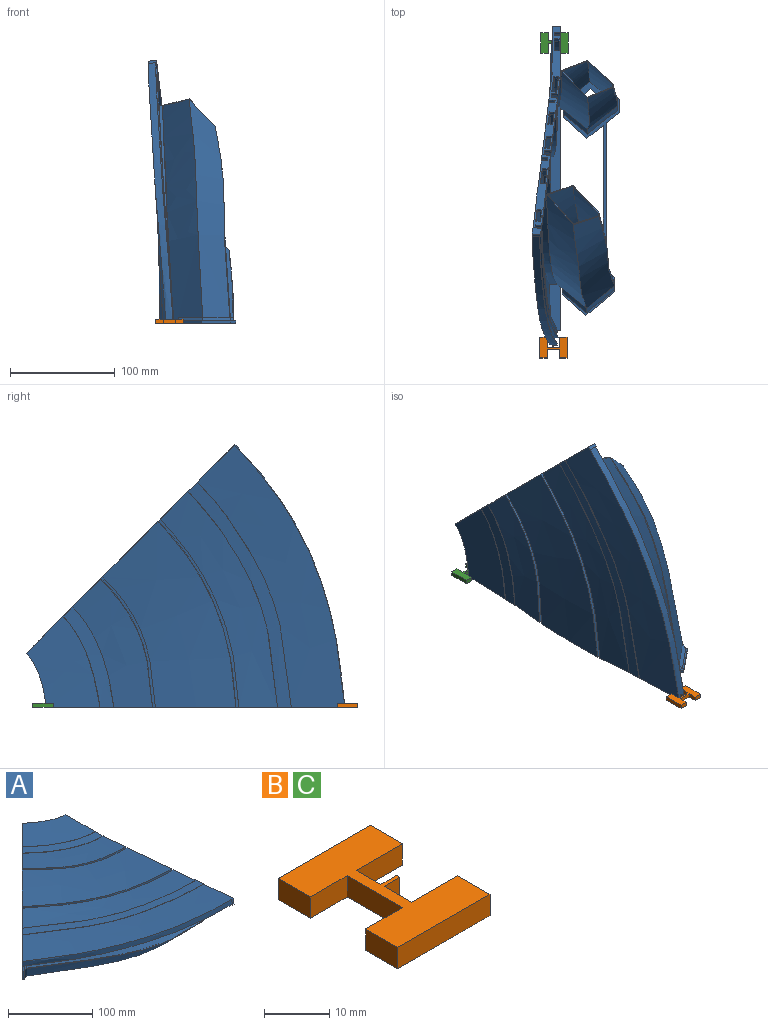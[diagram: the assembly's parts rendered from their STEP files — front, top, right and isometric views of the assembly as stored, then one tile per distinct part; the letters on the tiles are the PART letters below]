
ASSEMBLY  parts=3 mates=1
PART A: 239 faces, bbox 308.2x408.3x92.3 mm
  f0: plane 16.99x11.09mm, normal (0.56,0.56,-0.61), area 53.8mm2, adj f176,f189,f194,f237
  f1: plane 15.73x10.48mm, normal (-0.56,-0.56,-0.62), area 50mm2, adj f176,f194,f207,f237
  f2: plane 6.18x4.61mm, normal (-0.64,-0.76,0.07), area 18.6mm2, adj f3,f8,f93,f150,f234
  f3: bspline ~224.09x154.19mm, area 4266.2mm2, adj f2,f4,f5,f6,f38,f39,f93,f97
  f4: plane 6.18x4.61mm, normal (0.64,0.76,-0.07), area 18.6mm2, adj f3,f5,f6,f7,f234
  f5: plane 5.6x3.35mm, normal (0,-0.09,-1), area 13.8mm2, adj f3,f4,f6,f7,f96,f146
  f6: plane 0.35x0mm, normal (0,1,-0.09), area 0mm2, adj f3,f4,f5
  f7: plane 6.21x0.86mm, normal (-0.77,0.64,-0.06), area 2.6mm2, adj f4,f5,f96,f175
  f8: plane 6.37x2.71mm, normal (-0.77,0.64,-0.06), area 17.6mm2, adj f2,f93,f145,f174,f175
  f9: plane 6.18x4.77mm, normal (-0.71,-0.7,0.06), area 18.6mm2, adj f11,f13,f44,f233
  f10: plane 5.65x3mm, normal (0,-0.09,-1), area 13.5mm2, adj f44,f96,f148,f172,f232
  f11: plane 12.48x5.23mm, normal (0,-0.09,-1), area 30.1mm2, adj f9,f12,f13,f44,f156,f157
  f12: plane 9.48x0.11mm, normal (0,-1,0.09), area 0.1mm2, adj f11,f44,f157
  f13: plane 6.37x2.71mm, normal (-0.71,0.7,-0.06), area 19.1mm2, adj f9,f11,f43,f173
  f14: bspline ~224.09x118.25mm, area 679.4mm2, adj f15,f23,f28,f50,f111,f177,f229,f230
  f15: plane 0.65x0.19mm, normal (1,0,0), area 0.1mm2, adj f14,f26,f112,f229,f231
  f16: bspline ~224.09x143.33mm, area 3418.5mm2, adj f17,f26,f176,f182,f183,f209,f222,f223
  f17: bspline ~86.16x71.71mm, area 2834.7mm2, adj f16,f25,f223,f231
  f18: bspline ~224.09x141.31mm, area 2875.5mm2, adj f19,f24,f211,f231
  f19: bspline ~224.09x142.44mm, area 3385.1mm2, adj f18,f20,f176,f180,f181,f210,f211,f231
  f20: bspline ~224.09x147.72mm, area 2798.8mm2, adj f19,f21,f176,f180,f181,f210,f211,f231
  f21: bspline ~224.09x146.06mm, area 2158mm2, adj f20,f24,f211,f231
  f22: bspline ~224.09x146.38mm, area 2040.9mm2, adj f23,f25,f220,f231
  f23: bspline ~224.09x148.22mm, area 2729.5mm2, adj f14,f22,f176,f177,f178,f208,f221,f231
  f24: bspline ~60.82x36.49mm, area 175.9mm2, adj f18,f21,f211,f231
  f25: bspline ~94.05x52.79mm, area 270.9mm2, adj f17,f22,f194,f220,f223,f231
  f26: bspline ~224.09x118.34mm, area 680.7mm2, adj f15,f16,f39,f98,f182,f231
  f27: plane 3x0.2mm, normal (0,1,0), area 0.6mm2, adj f28,f229,f230,f231
  f28: plane 2.9x0.23mm, normal (0,0,1), area 0.4mm2, adj f14,f27,f230,f231
  f29: bspline ~276.75x124.81mm, area 1625.6mm2, adj f30,f47,f54,f102,f184,f224,f225,f227
  f30: plane 0.65x0.25mm, normal (1,0,0), area 0.1mm2, adj f29,f37,f114,f224,f228
  f31: bspline ~276.73x148.6mm, area 7464.5mm2, adj f36,f54,f218,f219,f228
  f32: bspline ~276.73x147.97mm, area 7399.6mm2, adj f35,f55,f198,f228
  f33: bspline ~276.78x147.28mm, area 6857mm2, adj f35,f56,f198,f228
  f34: bspline ~276.78x147.99mm, area 6842.5mm2, adj f36,f57,f216,f217,f228
  f35: bspline ~178.56x86.19mm, area 529.1mm2, adj f32,f33,f198,f228
  f36: bspline ~215.34x98.2mm, area 785.5mm2, adj f31,f34,f194,f216,f219,f228
  f37: bspline ~276.75x124.83mm, area 1611.3mm2, adj f30,f41,f57,f95,f182,f228
  f38: bspline ~116.31x50.29mm, area 805mm2, adj f3,f46,f147,f182
  f39: bspline ~224.09x123.83mm, area 610.4mm2, adj f3,f26,f98,f182
  f40: bspline ~237.46x97.92mm, area 1629.1mm2, adj f47,f52,f102,f184
  f41: bspline ~276.77x131.24mm, area 1236.1mm2, adj f37,f42,f95,f182
  f42: bspline ~276.82x162.37mm, area 7495.1mm2, adj f41,f48,f95,f113,f126,f165,f167,f168
  f43: bspline ~276.82x126.75mm, area 1185.4mm2, adj f13,f44,f45,f182
  f44: bspline ~276.82x267.27mm, area 11732.8mm2, adj f9,f10,f11,f12,f43,f49,f100,f129
  f45: bspline ~276.82x132.79mm, area 1180.7mm2, adj f43,f48,f96,f114,f173,f182
  f46: bspline ~224.09x124.52mm, area 792.9mm2, adj f38,f49,f96,f101,f145,f147,f174,f182
  f47: bspline ~302.64x168.04mm, area 10474.8mm2, adj f29,f40,f102,f124,f184
  f48: bspline ~276.82x126.75mm, area 1214.6mm2, adj f42,f45,f113,f182
  f49: bspline ~224.09x118.61mm, area 833.6mm2, adj f44,f46,f100,f182
  f50: bspline ~224.09x163.53mm, area 3353.3mm2, adj f14,f51,f111,f143,f177
  f51: bspline ~151.39x95.08mm, area 381.8mm2, adj f50,f53,f111,f177
  f52: bspline ~243.5x101.62mm, area 407.9mm2, adj f40,f74,f96,f114,f116,f176,f184,f185
  f53: bspline ~151.4x96.62mm, area 97.4mm2, adj f51,f70,f96,f112,f176,f177,f179
  f54: bspline ~276.75x149.56mm, area 8569.3mm2, adj f29,f31,f176,f184,f186,f196,f218,f228
  f55: bspline ~276.75x148.91mm, area 8407.6mm2, adj f32,f56,f176,f187,f188,f197,f198,f228
  f56: bspline ~276.78x148.91mm, area 7651.2mm2, adj f33,f55,f176,f187,f188,f197,f198,f228
  f57: bspline ~276.78x149.58mm, area 7742.4mm2, adj f34,f37,f176,f182,f183,f195,f217,f228
  f58: bspline ~302.64x127.67mm, area 469.7mm2, adj f59,f73,f117,f176
  f59: bspline ~302.64x127.24mm, area 1456.4mm2, adj f58,f60,f117,f176
  f60: bspline ~302.64x129.88mm, area 1230.4mm2, adj f59,f61,f117,f176
  f61: bspline ~302.64x126.08mm, area 1678.4mm2, adj f60,f62,f117,f176
  f62: bspline ~302.64x127.68mm, area 414.7mm2, adj f61,f69,f96,f119,f176
  f63: bspline ~302.64x129.68mm, area 1099.6mm2, adj f69,f74,f96,f116,f176
  f64: bspline ~151.4x99.28mm, area 253.5mm2, adj f70,f75,f96,f108,f110,f176
  f65: bspline ~151.4x95.54mm, area 363.1mm2, adj f66,f71,f105,f176
  f66: bspline ~151.4x99.51mm, area 237.9mm2, adj f65,f67,f105,f176
  f67: bspline ~151.41x96.89mm, area 290mm2, adj f66,f68,f105,f176
  f68: bspline ~151.41x97.35mm, area 88.4mm2, adj f67,f72,f105,f106,f176
  f69: bspline ~302.64x126.09mm, area 1689.6mm2, adj f62,f63,f96,f176
  f70: bspline ~151.4x95.12mm, area 408.2mm2, adj f53,f64,f96,f176
  f71: bspline ~56.3x27.06mm, area 91.4mm2, adj f65,f75,f96,f107,f109,f176
  f72: bspline ~151.41x95.65mm, area 393.3mm2, adj f68,f80,f96,f176
  f73: bspline ~302.64x125.97mm, area 1933.5mm2, adj f58,f92,f117,f176
  f74: bspline ~302.64x126.09mm, area 1651.4mm2, adj f52,f63,f115,f176
  f75: bspline ~151.4x95.51mm, area 370.3mm2, adj f64,f71,f108,f176
  f76: bspline ~224.09x121.96mm, area 404.2mm2, adj f77,f85,f96,f104,f161,f163,f176
  f77: bspline ~224.09x118.47mm, area 814mm2, adj f76,f86,f104,f162,f176
  f78: bspline ~276.82x129.93mm, area 596.8mm2, adj f79,f87,f96,f103,f159,f160,f176
  f79: bspline ~276.82x126.4mm, area 1182.6mm2, adj f78,f88,f103,f160,f176
  f80: bspline ~224.08x170.05mm, area 3821.1mm2, adj f72,f81,f96,f176
  f81: bspline ~224.08x117.14mm, area 28.7mm2, adj f80,f82,f96,f176
  f82: bspline ~224.08x130.11mm, area 1335.4mm2, adj f81,f83,f96,f176
  f83: bspline ~224.08x117.75mm, area 31.8mm2, adj f82,f84,f96,f176
  f84: bspline ~224.09x155.4mm, area 4709mm2, adj f83,f85,f96,f163,f176
  f85: bspline ~224.09x118.44mm, area 800.1mm2, adj f76,f84,f163,f176
  f86: bspline ~276.82x200.07mm, area 12673.9mm2, adj f77,f87,f96,f159,f162,f176
  f87: bspline ~276.82x126.4mm, area 1168.5mm2, adj f78,f86,f159,f176
  f88: bspline ~276.82x163.01mm, area 8024.3mm2, adj f79,f89,f96,f160,f176
  f89: bspline ~276.77x125.36mm, area 68.8mm2, adj f88,f90,f96,f176
  f90: bspline ~276.77x138.28mm, area 2986.8mm2, adj f89,f91,f96,f176
  f91: bspline ~276.74x125.31mm, area 71.8mm2, adj f90,f92,f96,f176
  f92: bspline ~252.35x161.9mm, area 13042.7mm2, adj f73,f91,f96,f118,f176
  f93: plane 12.61x5.23mm, normal (0,-0.09,-1), area 37.5mm2, adj f2,f3,f8,f97,f145,f147,f150,f158
  f94: plane 4.68x0.43mm, normal (-1,0,0), area 0.1mm2, adj f127,f165
  f95: plane 8.46x6.91mm, normal (-1,0,0), area 50.9mm2, adj f37,f41,f42,f114,f169
  f96: plane 282.81x27.27mm, normal (1,0,0), area 1616.1mm2, adj f5,f7,f10,f45,f46,f52,f53,f62
  f97: plane 16.3x5.14mm, normal (0,-1,-0.05), area 30.9mm2, adj f3,f93,f149,f151,f158
  f98: plane 34.01x8.65mm, normal (-1,0,0), area 112.2mm2, adj f3,f26,f39,f99,f112,f137,f138,f139
  f99: plane 28.24x3mm, normal (0,-0.09,-1), area 85mm2, adj f96,f98,f112,f146
  f100: plane 64x11.73mm, normal (-1,0,0), area 240.7mm2, adj f44,f49,f101,f130,f131,f132,f133,f135
  f101: plane 63.46x5.56mm, normal (0,-0.09,-1), area 191.1mm2, adj f46,f96,f100,f148
  f102: plane 43.34x9.96mm, normal (-1,0,0), area 193.5mm2, adj f29,f40,f47,f114,f121,f122,f123
  f103: plane 4.35x0.38mm, normal (-1,0,0), area 0.1mm2, adj f78,f79,f160
  f104: plane 4.08x0.36mm, normal (-1,0,0), area 0.1mm2, adj f76,f77,f161
  f105: plane 6.91x6.2mm, normal (-1,0,0), area 31.9mm2, adj f65,f66,f67,f68,f106,f107
  f106: plane 3.05x1.05mm, normal (0,1,0), area 3mm2, adj f68,f96,f105,f107
  f107: plane 7x3mm, normal (0,0,-1), area 20.9mm2, adj f71,f96,f105,f106
  f108: plane 6.2x0.09mm, normal (-1,0,0), area 0.6mm2, adj f64,f75,f109,f110
  f109: plane 3.01x0.1mm, normal (0,0,-1), area 0.1mm2, adj f71,f108,f110
  f110: plane 6.25x3.05mm, normal (0,-1,0), area 18.6mm2, adj f64,f96,f108,f109
  f111: plane 43.02x6.21mm, normal (-1,0,0), area 191.4mm2, adj f14,f50,f51,f112,f141,f142,f144
  f112: plane 49.44x3.01mm, normal (0,0,-1), area 148.1mm2, adj f15,f53,f96,f98,f99,f111
  f113: plane 8.16x6.84mm, normal (-1,0,0), area 47.4mm2, adj f42,f48,f114,f168
  f114: plane 85.23x7.47mm, normal (0,-0.09,-1), area 333.9mm2, adj f30,f45,f52,f95,f96,f102,f113,f168
  f115: plane 6.18x0.56mm, normal (-1,0,0), area 0.1mm2, adj f74,f116
  f116: plane 6.2x3.02mm, normal (0,-1,0.09), area 18.6mm2, adj f52,f63,f96,f115
  f117: plane 8.58x7.53mm, normal (-1,0,0), area 32.2mm2, adj f58,f59,f60,f61,f73,f118,f119
  f118: plane 7.99x3.02mm, normal (0,-1,0.09), area 24mm2, adj f92,f96,f117,f119
  f119: plane 7x3.01mm, normal (0,-0.09,-1), area 21mm2, adj f62,f96,f117,f118
  f120: plane 15.94x3mm, normal (0,-0.09,-1), area 48mm2, adj f96,f121,f123,f124
  f121: plane 4.68x3mm, normal (0,1,-0.09), area 14.1mm2, adj f96,f102,f120,f122,f124
  f122: plane 15.94x3mm, normal (0,0.09,1), area 48mm2, adj f96,f102,f121,f123
  f123: plane 4.68x3mm, normal (0,-1,0.09), area 14.1mm2, adj f96,f102,f120,f122,f124
  f124: plane 15.94x1.44mm, normal (1,0,0), area 0.8mm2, adj f47,f120,f121,f123
  f125: plane 4.68x3mm, normal (0,-1,0.09), area 14.1mm2, adj f96,f126,f128,f164
  f126: plane 20.73x3.01mm, normal (0,-0.09,-1), area 62.4mm2, adj f42,f96,f125,f127,f164
  f127: plane 4.68x3mm, normal (0,1,-0.09), area 14.1mm2, adj f94,f96,f126,f128
  f128: plane 20.73x3mm, normal (0,0.09,1), area 62.4mm2, adj f96,f125,f127,f166
  f129: plane 16.34x3mm, normal (0,-0.09,-1), area 49.2mm2, adj f44,f96,f130,f132
  f130: plane 4.68x3mm, normal (0,1,-0.09), area 14.1mm2, adj f96,f100,f129,f131
  f131: plane 16.34x3mm, normal (0,0.09,1), area 49.2mm2, adj f96,f100,f130,f132
  f132: plane 4.68x3mm, normal (0,-1,0.09), area 14.1mm2, adj f96,f100,f129,f131
  f133: plane 4.68x3mm, normal (0,-1,0.09), area 14.1mm2, adj f96,f100,f134,f136
  f134: plane 16.34x3mm, normal (0,-0.09,-1), area 49.2mm2, adj f44,f96,f133,f135
  f135: plane 4.68x3mm, normal (0,1,-0.09), area 14.1mm2, adj f96,f100,f134,f136
  f136: plane 16.34x3mm, normal (0,0.09,1), area 49.2mm2, adj f96,f100,f133,f135
  f137: plane 4.68x3mm, normal (0,1,-0.09), area 14.1mm2, adj f96,f98,f138,f140
  f138: plane 20.72x3mm, normal (0,0.09,1), area 62.4mm2, adj f96,f98,f137,f139
  f139: plane 4.68x3mm, normal (0,-1,0.09), area 14.1mm2, adj f96,f98,f138,f140
  f140: plane 20.73x3.01mm, normal (0,-0.09,-1), area 62.4mm2, adj f3,f96,f137,f139
  f141: plane 16x3mm, normal (0,0,1), area 48mm2, adj f96,f111,f142,f144
  f142: plane 4.7x3mm, normal (0,-1,0), area 14.1mm2, adj f96,f111,f141,f143
  f143: plane 16x3mm, normal (0,0,-1), area 48mm2, adj f50,f96,f142,f144
  f144: plane 4.7x3mm, normal (0,1,0), area 14.1mm2, adj f96,f111,f141,f143
  f145: plane 6.18x0.54mm, normal (0,1,-0.09), area 3.1mm2, adj f8,f46,f93,f147
  f146: plane 6.18x3mm, normal (0,-1,0.09), area 18.6mm2, adj f5,f96,f98,f99
  f147: plane 6.18x0.56mm, normal (1,0,0), area 0.1mm2, adj f38,f46,f93,f145
  f148: plane 6.18x3mm, normal (0,-1,0.09), area 18.6mm2, adj f10,f96,f100,f101
  f149: plane 6x2.49mm, normal (0,-0.09,-1), area 15mm2, adj f97,f150,f151,f158
  f150: plane 14.92x5.09mm, normal (0,1,-0.09), area 30.6mm2, adj f2,f3,f93,f149,f151,f158
  f151: plane 5.36x3.21mm, normal (-1,0,0), area 14.6mm2, adj f3,f97,f149,f150
  f152: plane 6.04x5mm, normal (0,1,-0.09), area 29.8mm2, adj f44,f154,f155,f157
  f153: plane 6.04x5.06mm, normal (0,-1,-0.05), area 30.1mm2, adj f44,f154,f155,f157
  f154: plane 6x2.49mm, normal (0,-0.09,-1), area 15mm2, adj f152,f153,f155,f157
  f155: plane 5.22x3.19mm, normal (-1,0,0), area 14.1mm2, adj f44,f152,f153,f154
  f156: plane 10.4x0.13mm, normal (0,1,-0.09), area 0.1mm2, adj f11,f44,f157
  f157: plane 5.24x3.19mm, normal (1,0,0), area 14.2mm2, adj f11,f12,f44,f152,f153,f154,f156
  f158: plane 5.26x3.19mm, normal (1,0,0), area 14.3mm2, adj f93,f97,f149,f150
  f159: bspline ~6x3mm, area 18.1mm2, adj f78,f86,f87,f96
  f160: plane 6.18x3.27mm, normal (0.08,0.99,-0.08), area 18.1mm2, adj f78,f79,f88,f96,f103
  f161: plane 4.11x3.01mm, normal (0.08,0.99,-0.08), area 12.3mm2, adj f76,f96,f104,f162
  f162: bspline ~3x1.93mm, area 5.7mm2, adj f77,f86,f96,f161
  f163: bspline ~6.6x3mm, area 18.1mm2, adj f76,f84,f85,f96
  f164: plane 4.69x0.43mm, normal (1,0,0), area 0.1mm2, adj f125,f126,f167
  f165: plane 9.2x4.76mm, normal (0,1,-0.09), area 31.8mm2, adj f42,f94,f166,f171
  f166: plane 20.72x4.44mm, normal (0,0.09,1), area 92mm2, adj f128,f165,f167,f171
  f167: plane 9.18x4.76mm, normal (0,-1,0.08), area 31.7mm2, adj f42,f164,f166,f171
  f168: plane 9.18x6.25mm, normal (0,1,-0.09), area 37.2mm2, adj f42,f113,f114,f170,f171
  f169: plane 9.2x6.25mm, normal (0,-1,0.09), area 37.3mm2, adj f42,f95,f114,f170,f171
  f170: plane 25.68x2.32mm, normal (-1,0,0), area 2.2mm2, adj f114,f168,f169,f171
  f171: bspline ~26.21x8.27mm, area 84.7mm2, adj f42,f165,f166,f167,f168,f169,f170
  f172: plane 6.21x0.9mm, normal (-0.71,0.7,-0.06), area 3.2mm2, adj f10,f96,f173,f232
  f173: plane 3.01x3.01mm, normal (0,-0.09,-1), area 4.5mm2, adj f13,f45,f96,f172,f233
  f174: plane 2.51x0.01mm, normal (0,-1,0.09), area 0mm2, adj f8,f46,f175
  f175: plane 2.99x2.5mm, normal (0,-0.09,-1), area 3.8mm2, adj f7,f8,f96,f174,f234
  f176: plane 204.05x204.05mm, normal (-0.71,0.71,0), area 6899.8mm2, adj f0,f1,f16,f19,f20,f23,f52,f53
  f177: plane 31.55x31.55mm, normal (0.71,-0.71,0), area 347.7mm2, adj f14,f23,f50,f51,f53,f178,f179
  f178: plane 31.61x31.46mm, normal (0,0,-1), area 101.3mm2, adj f23,f176,f177,f179
  f179: plane 1.7x1.7mm, normal (0.71,0.71,0), area 3.1mm2, adj f53,f176,f177,f178
  f180: plane 0.98x0.98mm, normal (0.71,-0.71,0), area 0.6mm2, adj f19,f20,f181
  f181: plane 3.01x2.53mm, normal (0,0,-1), area 3.6mm2, adj f19,f20,f176,f180
  f182: plane 120.26x120.26mm, normal (0.71,-0.71,0), area 2119.1mm2, adj f3,f16,f26,f37,f38,f39,f41,f42
  f183: plane 118.46x117.78mm, normal (0,0,-1), area 395.1mm2, adj f16,f57,f176,f182
  f184: plane 32.76x32.76mm, normal (0.71,-0.71,0), area 442.2mm2, adj f29,f40,f47,f52,f54,f185,f186
  f185: plane 2.97x1.79mm, normal (-0.71,-0.71,-0.04), area 6.9mm2, adj f52,f176,f184,f186
  f186: plane 31.02x30.84mm, normal (0,0,-1), area 99.2mm2, adj f54,f176,f184,f185
  f187: plane 3.76x3.76mm, normal (0.71,-0.71,0), area 8.7mm2, adj f55,f56,f188
  f188: plane 5.65x5.12mm, normal (0,0,-1), area 12.5mm2, adj f55,f56,f176,f187
  f189: plane 21.92x14.87mm, normal (0.55,0.55,0.64), area 83.9mm2, adj f0,f176,f194,f195,f216,f217
  f190: plane 8.01x6.16mm, normal (0.56,0.56,-0.61), area 25.4mm2, adj f176,f191,f194,f238
  f191: plane 11.69x11.69mm, normal (0,0,-1), area 35.1mm2, adj f176,f190,f192,f194
  f192: plane 27.66x17.72mm, normal (-0.55,-0.55,-0.63), area 89.2mm2, adj f176,f191,f193,f194
  f193: plane 22.71x15.87mm, normal (-0.53,-0.53,0.66), area 75.6mm2, adj f176,f192,f194,f196
  f194: plane 168.64x168.64mm, normal (0.71,-0.71,0), area 801.4mm2, adj f0,f1,f25,f36,f189,f190,f191,f192
  f195: plane 7.46x5.87mm, normal (0.02,0.02,1), area 23.3mm2, adj f57,f176,f189,f217
  f196: plane 8.31x5.61mm, normal (0.02,0.02,1), area 20.4mm2, adj f54,f176,f193,f194,f218
  f197: plane 7.74x7.18mm, normal (0.02,0.02,1), area 20.1mm2, adj f55,f56,f176,f198
  f198: plane 49.49x32.32mm, normal (0.71,-0.71,0), area 722.5mm2, adj f32,f33,f35,f55,f56,f197,f199,f200
  f199: plane 16.34x12.16mm, normal (0.53,0.53,0.67), area 54.9mm2, adj f176,f198,f200,f202
  f200: plane 16.87x13.16mm, normal (-0.51,-0.51,0.69), area 58.3mm2, adj f176,f198,f199,f201
  f201: plane 17.34x13.24mm, normal (-0.52,-0.52,-0.68), area 59.4mm2, adj f176,f198,f200,f202
  f202: plane 17.87x12.08mm, normal (0.55,0.55,-0.63), area 57.7mm2, adj f176,f198,f199,f201
  f203: plane 25.56x16.62mm, normal (0.55,0.55,0.63), area 82.7mm2, adj f176,f194,f204,f208
  f204: plane 28.52x18.48mm, normal (0.54,0.54,-0.64), area 92.6mm2, adj f176,f194,f203,f205
  f205: plane 10.85x10.85mm, normal (0,0,-1), area 32.1mm2, adj f176,f194,f204,f206
  f206: plane 12.73x8.82mm, normal (-0.56,-0.56,-0.62), area 40.4mm2, adj f176,f194,f205,f238
  f207: plane 22.62x15.97mm, normal (-0.53,-0.53,0.66), area 75.6mm2, adj f1,f176,f194,f209
  f208: plane 8.17x5.95mm, normal (0,0,1), area 23.6mm2, adj f23,f176,f194,f203,f221
  f209: plane 9.1x6.26mm, normal (0,0,1), area 22.2mm2, adj f16,f176,f194,f207,f222
  f210: plane 5.94x5.44mm, normal (0,0,1), area 13.9mm2, adj f19,f20,f176,f211
  f211: plane 51.32x32.09mm, normal (0.71,-0.71,0), area 717.3mm2, adj f18,f19,f20,f21,f24,f210,f212,f213
  f212: plane 19.2x12.4mm, normal (0.56,0.56,0.62), area 61mm2, adj f176,f211,f213,f215
  f213: plane 16.58x12.24mm, normal (-0.53,-0.53,0.67), area 55.6mm2, adj f176,f211,f212,f214
  f214: plane 18.81x13.61mm, normal (-0.53,-0.53,-0.66), area 63mm2, adj f176,f211,f213,f215
  f215: plane 16.19x11.04mm, normal (0.55,0.55,-0.63), area 52.1mm2, adj f176,f211,f212,f214
  f216: bspline ~31.85x21mm, area 180.2mm2, adj f34,f36,f189,f194,f217
  f217: bspline ~28.7x20.23mm, area 129.4mm2, adj f34,f57,f189,f195,f216
  f218: bspline ~30.25x20.4mm, area 140.9mm2, adj f31,f54,f194,f196,f219
  f219: bspline ~30.78x20.66mm, area 156.2mm2, adj f31,f36,f194,f218
  f220: bspline ~30.8x21.01mm, area 177.9mm2, adj f22,f25,f194,f221
  f221: bspline ~32.64x22.49mm, area 171.2mm2, adj f23,f194,f208,f220
  f222: bspline ~27.6x18.64mm, area 137.5mm2, adj f16,f194,f209,f223
  f223: bspline ~35.84x23.02mm, area 171.2mm2, adj f16,f17,f25,f194,f222
  f224: plane 3x0.1mm, normal (0,-0.09,-1), area 0.2mm2, adj f29,f30,f226,f227
  f225: plane 2.8x0.07mm, normal (0,0.05,1), area 0.1mm2, adj f29,f226,f227,f228
  f226: plane 3x0.34mm, normal (0,-1,0.09), area 1mm2, adj f224,f225,f227,f228
  f227: plane 0.35x0.06mm, normal (1,0,0), area 0mm2, adj f29,f224,f225,f226
  f228: plane 51.47x51.31mm, normal (0.87,-0.04,-0.5), area 111.5mm2, adj f29,f30,f31,f32,f33,f34,f35,f36
  f229: plane 3x0.23mm, normal (0,0,-1), area 0.4mm2, adj f14,f15,f27,f230
  f230: plane 0.23x0.2mm, normal (1,0,0), area 0mm2, adj f14,f27,f28,f229
  f231: plane 51.56x50.84mm, normal (0.89,0,-0.45), area 106.8mm2, adj f14,f15,f16,f17,f18,f19,f20,f21
  f232: plane 6.18x4.77mm, normal (0.71,0.7,-0.06), area 18.6mm2, adj f10,f44,f172,f233
  f233: plane 5.85x5.23mm, normal (-0.51,0.45,-0.74), area 5.6mm2, adj f9,f44,f173,f232
  f234: plane 5.89x5.06mm, normal (-0.55,0.4,-0.73), area 5.7mm2, adj f2,f3,f4,f175,f235,f236
  f235: plane 0.69x0.58mm, normal (0.77,-0.64,0.06), area 0mm2, adj f3,f234,f236
  f236: plane 0x0mm, normal (-0.64,-0.76,0.07), area 0mm2, adj f3,f234,f235
  f237: plane 98.44x98.44mm, normal (0,0,1), area 341.8mm2, adj f0,f1,f176,f194
  f238: plane 101.75x101.75mm, normal (0,0,-1), area 353.5mm2, adj f176,f190,f194,f206
PART B: 18 faces, bbox 20x26x4 mm
  f0: plane 10x4mm, normal (0,1,0), area 40mm2, adj f1,f15,f16,f17
  f1: plane 6x4mm, normal (1,0,0), area 24mm2, adj f0,f2,f16,f17
  f2: plane 4x3.44mm, normal (0,-1,0), area 13.7mm2, adj f1,f3,f16,f17
  f3: plane 4x0.7mm, normal (1,0,0), area 2.8mm2, adj f2,f4,f16,f17
  f4: plane 4x3.44mm, normal (0,1,0), area 13.7mm2, adj f3,f5,f16,f17
  f5: plane 5.3x4mm, normal (1,0,0), area 21.2mm2, adj f4,f6,f16,f17
  f6: plane 10x4mm, normal (0,-1,0), area 40mm2, adj f5,f7,f16,f17
  f7: plane 7x4mm, normal (1,0,0), area 28mm2, adj f6,f8,f16,f17
  f8: plane 20x4mm, normal (0,1,0), area 80mm2, adj f7,f9,f16,f17
  f9: plane 7x4mm, normal (-1,0,0), area 28mm2, adj f8,f10,f16,f17
  f10: plane 8x4mm, normal (0,-1,0), area 32mm2, adj f9,f11,f16,f17
  f11: plane 12x4mm, normal (-1,0,0), area 48mm2, adj f10,f12,f16,f17
  f12: plane 8x4mm, normal (0,1,0), area 32mm2, adj f11,f13,f16,f17
  f13: plane 7x4mm, normal (-1,0,0), area 28mm2, adj f12,f14,f16,f17
  f14: plane 20x4mm, normal (0,-1,0), area 80mm2, adj f13,f15,f16,f17
  f15: plane 7x4mm, normal (1,0,0), area 28mm2, adj f0,f14,f16,f17
  f16: plane 26x20mm, normal (0,0,1), area 306.4mm2, adj f0,f1,f2,f3,f4,f5,f6,f7
  f17: plane 26x20mm, normal (0,0,-1), area 306.4mm2, adj f0,f1,f2,f3,f4,f5,f6,f7
PART C: same geometry as B
PLACE A rot(axis=(-0.36,-0.86,0.36),98.4deg) t=(-20.11,136.44,12.94)mm fixed
PLACE B rot(axis=(0,0,1),90deg) t=(16.68,34.83,12.94)mm fixed
PLACE C rot(axis=(0,0,-1),90deg) t=(-50.04,239.04,12.94)mm
MATE planar C.f17 <-> A.f176  axis (0,0,-1) through (-15.83,279.19,12.94)mm
